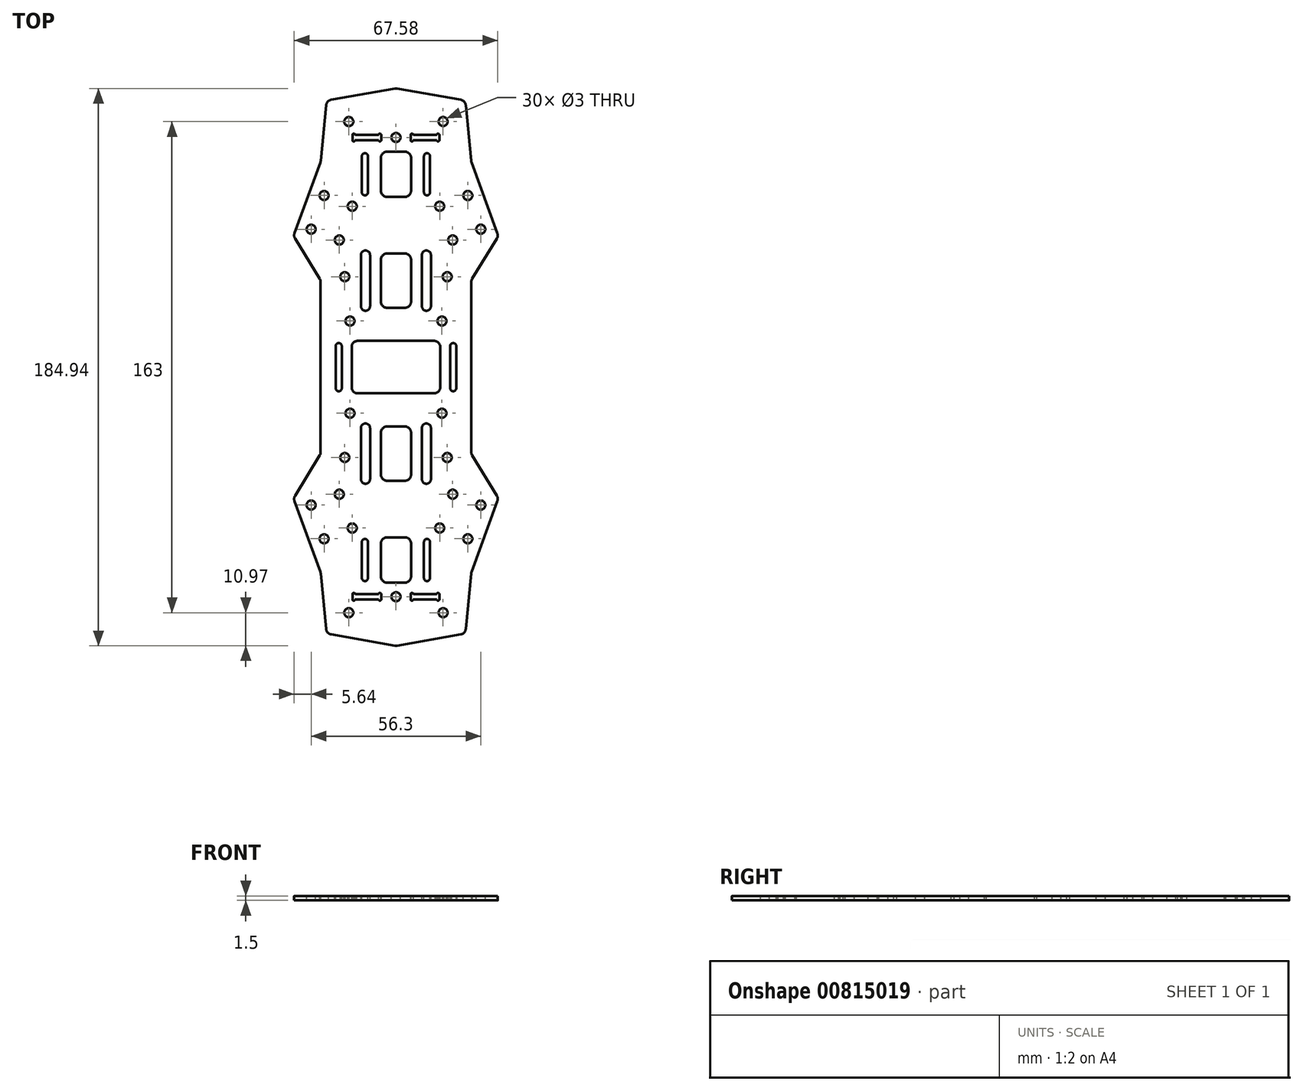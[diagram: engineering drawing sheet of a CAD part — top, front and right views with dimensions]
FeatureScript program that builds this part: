
annotation { "Feature Type Name" : "Feature", "Feature Type Description" : "" }
export const myFeature = defineFeature(function(context is Context, id is Id, definition is map)
    precondition{}
    {
        {
            var Q0;
            Q0=qCreatedBy(makeId("Top.planeOp"),FACE);
            var sketch = newSketch(context, id + "F0", { "sketchPlane" : qUnion([Q0])});
            skLineSegment(sketch, "E0.0.14", {"start": v(-25, 92.5) * mm, "end": v(-25, 63.7) * mm});
            skLineSegment(sketch, "E0.0.16", {"start": v(-25, 63.7) * mm, "end": v(-34, 49) * mm});
            skLineSegment(sketch, "E0.0.18", {"start": v(-34, 49) * mm, "end": v(-25, 24.3) * mm});
            skLineSegment(sketch, "E0.0.20", {"start": v(-25, 24.3) * mm, "end": v(-23, 4.06) * mm});
            skLineSegment(sketch, "E0.0.22", {"start": v(-23, 4.06) * mm, "end": v(0, 0) * mm});
            skLineSegment(sketch, "E0.0.23", {"start": v(0, 0) * mm, "end": v(23, 4.06) * mm});
            skLineSegment(sketch, "E0.0.25", {"start": v(23, 4.06) * mm, "end": v(25, 24.3) * mm});
            skLineSegment(sketch, "E0.0.27", {"start": v(25, 24.3) * mm, "end": v(34, 49) * mm});
            skLineSegment(sketch, "E0.0.29", {"start": v(34, 49) * mm, "end": v(25, 63.7) * mm});
            skLineSegment(sketch, "E0.0.31", {"start": v(25, 63.7) * mm, "end": v(25, 92.5) * mm});
            skLineSegment(sketch, "E1.bottom", {"start": v(34, 0) * mm, "end": v(-34, 0) * mm, "construction": true});
            skLineSegment(sketch, "E1.top", {"start": v(34, 185) * mm, "end": v(-34, 185) * mm, "construction": true});
            skLineSegment(sketch, "E1.left", {"start": v(-34, 0) * mm, "end": v(-34, 185) * mm, "construction": true});
            skLineSegment(sketch, "E1.right", {"start": v(34, 0) * mm, "end": v(34, 185) * mm, "construction": true});
            skPoint(sketch, "E2", {"position": v(0, 0) * mm});
            skLineSegment(sketch, "E3", {"start": v(0, 185) * mm, "end": v(0, 0) * mm, "construction": true});
            skLineSegment(sketch, "E4", {"start": v(-34, 92.5) * mm, "end": v(34, 92.5) * mm, "construction": true});
            skLineSegment(sketch, "E5.MirrorCS", {"start": v(-25, 92.5) * mm, "end": v(-25, 121.3) * mm});
            skLineSegment(sketch, "E6.MirrorCS", {"start": v(25, 121.3) * mm, "end": v(25, 92.5) * mm});
            skLineSegment(sketch, "E7.MirrorCS", {"start": v(34, 136) * mm, "end": v(25, 121.3) * mm});
            skLineSegment(sketch, "E8.MirrorCS", {"start": v(25, 160.7) * mm, "end": v(34, 136) * mm});
            skLineSegment(sketch, "E9.MirrorCS", {"start": v(23, 180.94) * mm, "end": v(25, 160.7) * mm});
            skLineSegment(sketch, "E10.MirrorCS", {"start": v(0, 185) * mm, "end": v(23, 180.94) * mm});
            skLineSegment(sketch, "E11.MirrorCS", {"start": v(-23, 180.94) * mm, "end": v(0, 185) * mm});
            skLineSegment(sketch, "E12.MirrorCS", {"start": v(-25, 160.7) * mm, "end": v(-23, 180.94) * mm});
            skLineSegment(sketch, "E13.MirrorCS", {"start": v(-34, 136) * mm, "end": v(-25, 160.7) * mm});
            skLineSegment(sketch, "E14.MirrorCS", {"start": v(-25, 121.3) * mm, "end": v(-34, 136) * mm});
            skPoint(sketch, "E15", {"position": v(0, 185) * mm});
            skSolve(sketch);
        }
        {
            var Q0;
            Q0=qSketchRegion(id+"F0",true);
            extrude(context, id + "F1", {"entities" : qUnion([Q0]), "depth" : 1.5 * mm, "offsetDistance" : 25 * mm});
        }
        {
            var Q0;
            Q0=makeQuery(id+"F1.opExtrude","CAP_FACE",FACE,{"disambiguationData":[OSD([sQuery(id+"F0.wireOp",EDGE,"E0.0.1"),sQuery(id+"F0.wireOp",EDGE,"E0.0.3"),sQuery(id+"F0.wireOp",EDGE,"E0.0.5"),sQuery(id+"F0.wireOp",EDGE,"E0.0.6"),sQuery(id+"F0.wireOp",EDGE,"E0.0.8"),sQuery(id+"F0.wireOp",EDGE,"E0.0.10"),sQuery(id+"F0.wireOp",EDGE,"E0.0.12"),sQuery(id+"F0.wireOp",EDGE,"E0.0.14"),sQuery(id+"F0.wireOp",EDGE,"E0.0.16"),sQuery(id+"F0.wireOp",EDGE,"E0.0.18"),sQuery(id+"F0.wireOp",EDGE,"E0.0.20"),sQuery(id+"F0.wireOp",EDGE,"E0.0.22"),sQuery(id+"F0.wireOp",EDGE,"E0.0.23"),sQuery(id+"F0.wireOp",EDGE,"E0.0.25"),sQuery(id+"F0.wireOp",EDGE,"E0.0.27"),sQuery(id+"F0.wireOp",EDGE,"E0.0.29"),sQuery(id+"F0.wireOp",EDGE,"E0.0.31"),sQuery(id+"F0.wireOp",EDGE,"E0.0.33")])],"isStart":false});
            var sketch = newSketch(context, id + "F2", { "sketchPlane" : qUnion([Q0])});
            skCircle(sketch, "E16.0", {"center": v(-15.65, 11) * mm, "radius": 1.5 * mm});
            skCircle(sketch, "E17.0", {"center": v(0, 16.3) * mm, "radius": 1.5 * mm});
            skCircle(sketch, "E17.9", {"center": v(15.65, 11) * mm, "radius": 1.5 * mm});
            skCircle(sketch, "E18.1", {"center": v(-23.85, 35.53) * mm, "radius": 1.5 * mm});
            skCircle(sketch, "E18.2", {"center": v(-28.15, 46.73) * mm, "radius": 1.5 * mm});
            skCircle(sketch, "E18.3", {"center": v(-14.51, 39.11) * mm, "radius": 1.5 * mm});
            skCircle(sketch, "E18.4", {"center": v(-18.81, 50.32) * mm, "radius": 1.5 * mm});
            skCircle(sketch, "E19.0", {"center": v(-17, 62.5) * mm, "radius": 1.5 * mm});
            skLineSegment(sketch, "E20", {"start": v(-10.3, 34.5) * mm, "end": v(-10.3, 22.5) * mm, "construction": true});
            skArc(sketch, "E21.0.startCap", {"start": v(-11.3, 34.5) * mm, "mid": v(-10.3, 35.5) * mm, "end": v(-9.3, 34.5) * mm});
            skArc(sketch, "E21.0.endCap", {"start": v(-9.3, 22.5) * mm, "mid": v(-10.3, 21.5) * mm, "end": v(-11.3, 22.5) * mm});
            skLineSegment(sketch, "E21.0.left", {"start": v(-9.3, 34.5) * mm, "end": v(-9.3, 22.5) * mm});
            skLineSegment(sketch, "E21.0.right", {"start": v(-11.3, 34.5) * mm, "end": v(-11.3, 22.5) * mm});
            skLineSegment(sketch, "E22", {"start": v(-19, 99.5) * mm, "end": v(-19, 85.5) * mm, "construction": true});
            skArc(sketch, "E23.0.startCap", {"start": v(-20, 99.5) * mm, "mid": v(-19, 100.5) * mm, "end": v(-18, 99.5) * mm});
            skArc(sketch, "E23.0.endCap", {"start": v(-18, 85.5) * mm, "mid": v(-19, 84.5) * mm, "end": v(-20, 85.5) * mm});
            skLineSegment(sketch, "E23.0.left", {"start": v(-18, 99.5) * mm, "end": v(-18, 85.5) * mm});
            skLineSegment(sketch, "E23.0.right", {"start": v(-20, 99.5) * mm, "end": v(-20, 85.5) * mm});
            skLineSegment(sketch, "E24.bottom", {"start": v(5, 21) * mm, "end": v(-5, 21) * mm});
            skLineSegment(sketch, "E24.top", {"start": v(5, 36) * mm, "end": v(-5, 36) * mm});
            skLineSegment(sketch, "E24.left", {"start": v(5, 21) * mm, "end": v(5, 36) * mm});
            skLineSegment(sketch, "E24.right", {"start": v(-5, 21) * mm, "end": v(-5, 36) * mm});
            skPoint(sketch, "E24.middle", {"position": v(0, 28.5) * mm});
            skLineSegment(sketch, "E25", {"start": v(0, 0) * mm, "end": v(0, 185) * mm, "construction": true});
            skLineSegment(sketch, "E26", {"start": v(61.94, 0) * mm, "end": v(-64, 0) * mm, "construction": true});
            skLineSegment(sketch, "E27", {"start": v(-46.28, 185) * mm, "end": v(44.52, 185) * mm, "construction": true});
            skPoint(sketch, "E28", {"position": v(0, 92.5) * mm});
            skLineSegment(sketch, "E29", {"start": v(-80.28, 92.5) * mm, "end": v(79, 92.5) * mm, "construction": true});
            skLineSegment(sketch, "E30", {"start": v(-10.1, 72.3) * mm, "end": v(-10.1, 55.3) * mm, "construction": true});
            skArc(sketch, "E31.0.startCap", {"start": v(-11.6, 72.3) * mm, "mid": v(-10.1, 73.8) * mm, "end": v(-8.6, 72.3) * mm});
            skArc(sketch, "E31.0.endCap", {"start": v(-8.6, 55.3) * mm, "mid": v(-10.1, 53.8) * mm, "end": v(-11.6, 55.3) * mm});
            skLineSegment(sketch, "E31.0.left", {"start": v(-8.6, 72.3) * mm, "end": v(-8.6, 55.3) * mm});
            skLineSegment(sketch, "E31.0.right", {"start": v(-11.6, 72.3) * mm, "end": v(-11.6, 55.3) * mm});
            skLineSegment(sketch, "E32.bottom", {"start": v(5, 54.8) * mm, "end": v(-5, 54.8) * mm});
            skLineSegment(sketch, "E32.top", {"start": v(5, 72.8) * mm, "end": v(-5, 72.8) * mm});
            skLineSegment(sketch, "E32.left", {"start": v(5, 54.8) * mm, "end": v(5, 72.8) * mm});
            skLineSegment(sketch, "E32.right", {"start": v(-5, 54.8) * mm, "end": v(-5, 72.8) * mm});
            skPoint(sketch, "E32.middle", {"position": v(0, 63.8) * mm});
            skArc(sketch, "E33.MirrorCS", {"start": v(-18, 99.5) * mm, "mid": v(-19, 100.5) * mm, "end": v(-20, 99.5) * mm});
            skArc(sketch, "E34.MirrorCS", {"start": v(-20, 85.5) * mm, "mid": v(-19, 84.5) * mm, "end": v(-18, 85.5) * mm});
            skLineSegment(sketch, "E35.bottom", {"start": v(14.7, 83.8) * mm, "end": v(-14.7, 83.8) * mm});
            skLineSegment(sketch, "E35.top", {"start": v(14.7, 101.2) * mm, "end": v(-14.7, 101.2) * mm});
            skLineSegment(sketch, "E35.left", {"start": v(14.7, 83.8) * mm, "end": v(14.7, 101.2) * mm});
            skLineSegment(sketch, "E35.right", {"start": v(-14.7, 83.8) * mm, "end": v(-14.7, 101.2) * mm});
            skCircle(sketch, "E36", {"center": v(-15.25, 77.2) * mm, "radius": 1.5 * mm});
            skLineSegment(sketch, "E37", {"start": v(-13.98, 17.18) * mm, "end": v(-13.98, 15.43) * mm, "construction": true});
            skArc(sketch, "E38.0.startCap", {"start": v(-14.4, 17.18) * mm, "mid": v(-13.98, 17.6) * mm, "end": v(-13.55, 17.18) * mm});
            skArc(sketch, "E38.0.endCap", {"start": v(-13.55, 15.43) * mm, "mid": v(-13.98, 15) * mm, "end": v(-14.4, 15.43) * mm});
            skLineSegment(sketch, "E38.0.left", {"start": v(-13.55, 17.18) * mm, "end": v(-13.55, 15.43) * mm});
            skLineSegment(sketch, "E38.0.right", {"start": v(-14.4, 17.18) * mm, "end": v(-14.4, 15.43) * mm});
            skLineSegment(sketch, "E39", {"start": v(-5.33, 17.18) * mm, "end": v(-5.33, 15.43) * mm, "construction": true});
            skArc(sketch, "E40.0.startCap", {"start": v(-5.75, 17.18) * mm, "mid": v(-5.33, 17.6) * mm, "end": v(-4.9, 17.18) * mm});
            skArc(sketch, "E40.0.endCap", {"start": v(-4.9, 15.43) * mm, "mid": v(-5.33, 15) * mm, "end": v(-5.75, 15.43) * mm});
            skLineSegment(sketch, "E40.0.left", {"start": v(-4.9, 17.18) * mm, "end": v(-4.9, 15.43) * mm});
            skLineSegment(sketch, "E40.0.right", {"start": v(-5.75, 17.18) * mm, "end": v(-5.75, 15.43) * mm});
            skLineSegment(sketch, "E41", {"start": v(-13.55, 17.18) * mm, "end": v(-5.75, 17.18) * mm});
            skLineSegment(sketch, "E42", {"start": v(-13.55, 15.43) * mm, "end": v(-5.75, 15.43) * mm});
            skLineSegment(sketch, "E43", {"start": v(-13.55, 15.43) * mm, "end": v(-5.75, 17.18) * mm, "construction": true});
            skPoint(sketch, "E44", {"position": v(-9.65, 16.3) * mm});
            skArc(sketch, "E45.MirrorCS", {"start": v(13.55, 15.43) * mm, "mid": v(13.97, 15) * mm, "end": v(14.4, 15.43) * mm});
            skArc(sketch, "E46.MirrorCS", {"start": v(4.9, 15.43) * mm, "mid": v(5.32, 15) * mm, "end": v(5.75, 15.43) * mm});
            skLineSegment(sketch, "E47.MirrorCS", {"start": v(13.55, 15.43) * mm, "end": v(5.75, 15.43) * mm});
            skLineSegment(sketch, "E48.MirrorCS", {"start": v(4.9, 17.18) * mm, "end": v(4.9, 15.43) * mm});
            skArc(sketch, "E49.MirrorCS", {"start": v(5.75, 17.18) * mm, "mid": v(5.32, 17.6) * mm, "end": v(4.9, 17.18) * mm});
            skLineSegment(sketch, "E50.MirrorCS", {"start": v(5.32, 17.18) * mm, "end": v(5.32, 15.43) * mm, "construction": true});
            skLineSegment(sketch, "E51.MirrorCS", {"start": v(5.75, 17.18) * mm, "end": v(5.75, 15.43) * mm});
            skLineSegment(sketch, "E52.MirrorCS", {"start": v(13.55, 15.43) * mm, "end": v(5.75, 17.18) * mm, "construction": true});
            skLineSegment(sketch, "E53.MirrorCS", {"start": v(13.97, 17.18) * mm, "end": v(13.97, 15.43) * mm, "construction": true});
            skPoint(sketch, "E54.MirrorP", {"position": v(9.65, 16.3) * mm});
            skLineSegment(sketch, "E55.MirrorCS", {"start": v(14.4, 17.18) * mm, "end": v(14.4, 15.43) * mm});
            skLineSegment(sketch, "E56.MirrorCS", {"start": v(13.55, 17.18) * mm, "end": v(5.75, 17.18) * mm});
            skArc(sketch, "E57.MirrorCS", {"start": v(14.4, 17.18) * mm, "mid": v(13.97, 17.6) * mm, "end": v(13.55, 17.18) * mm});
            skLineSegment(sketch, "E58.MirrorCS", {"start": v(13.55, 17.18) * mm, "end": v(13.55, 15.43) * mm});
            skPoint(sketch, "E59", {"position": v(-10.3, 28.5) * mm});
            skArc(sketch, "E60.MirrorCS", {"start": v(9.3, 22.5) * mm, "mid": v(10.3, 21.5) * mm, "end": v(11.3, 22.5) * mm});
            skArc(sketch, "E61.MirrorCS", {"start": v(11.3, 34.5) * mm, "mid": v(10.3, 35.5) * mm, "end": v(9.3, 34.5) * mm});
            skLineSegment(sketch, "E62.MirrorCS", {"start": v(11.3, 34.5) * mm, "end": v(11.3, 22.5) * mm});
            skLineSegment(sketch, "E63.MirrorCS", {"start": v(10.3, 34.5) * mm, "end": v(10.3, 22.5) * mm, "construction": true});
            skPoint(sketch, "E64.MirrorP", {"position": v(10.3, 28.5) * mm});
            skLineSegment(sketch, "E65.MirrorCS", {"start": v(9.3, 34.5) * mm, "end": v(9.3, 22.5) * mm});
            skLineSegment(sketch, "E66.bottom", {"start": v(-23.85, 35.53) * mm, "end": v(-28.15, 46.73) * mm, "construction": true});
            skLineSegment(sketch, "E66.top", {"start": v(-14.51, 39.11) * mm, "end": v(-18.81, 50.32) * mm, "construction": true});
            skLineSegment(sketch, "E66.left", {"start": v(-23.85, 35.53) * mm, "end": v(-14.51, 39.11) * mm, "construction": true});
            skLineSegment(sketch, "E66.right", {"start": v(-28.15, 46.73) * mm, "end": v(-18.81, 50.32) * mm, "construction": true});
            skPoint(sketch, "E66.middle", {"position": v(-21.33, 42.92) * mm});
            skPoint(sketch, "E67.MirrorP", {"position": v(21.33, 42.92) * mm});
            skCircle(sketch, "E68.MirrorC", {"center": v(18.81, 50.32) * mm, "radius": 1.5 * mm});
            skCircle(sketch, "E69.MirrorC", {"center": v(28.15, 46.73) * mm, "radius": 1.5 * mm});
            skCircle(sketch, "E70.MirrorC", {"center": v(14.51, 39.11) * mm, "radius": 1.5 * mm});
            skCircle(sketch, "E71.MirrorC", {"center": v(23.85, 35.53) * mm, "radius": 1.5 * mm});
            skPoint(sketch, "E72", {"position": v(-10.1, 63.8) * mm});
            skPoint(sketch, "E73.MirrorP", {"position": v(10.1, 63.8) * mm});
            skArc(sketch, "E74.MirrorCS", {"start": v(11.6, 72.3) * mm, "mid": v(10.1, 73.8) * mm, "end": v(8.6, 72.3) * mm});
            skLineSegment(sketch, "E75.MirrorCS", {"start": v(11.6, 72.3) * mm, "end": v(11.6, 55.3) * mm});
            skLineSegment(sketch, "E76.MirrorCS", {"start": v(8.6, 72.3) * mm, "end": v(8.6, 55.3) * mm});
            skArc(sketch, "E77.MirrorCS", {"start": v(8.6, 55.3) * mm, "mid": v(10.1, 53.8) * mm, "end": v(11.6, 55.3) * mm});
            skLineSegment(sketch, "E78.MirrorCS", {"start": v(10.1, 72.3) * mm, "end": v(10.1, 55.3) * mm, "construction": true});
            skCircle(sketch, "E79.MirrorC", {"center": v(17, 62.5) * mm, "radius": 1.5 * mm});
            skLineSegment(sketch, "E80.MirrorCS", {"start": v(20, 99.5) * mm, "end": v(20, 85.5) * mm});
            skArc(sketch, "E81.MirrorCS", {"start": v(18, 99.5) * mm, "mid": v(19, 100.5) * mm, "end": v(20, 99.5) * mm});
            skLineSegment(sketch, "E82.MirrorCS", {"start": v(18, 99.5) * mm, "end": v(18, 85.5) * mm});
            skArc(sketch, "E83.MirrorCS", {"start": v(18, 85.5) * mm, "mid": v(19, 84.5) * mm, "end": v(20, 85.5) * mm});
            skArc(sketch, "E84.MirrorCS", {"start": v(20, 85.5) * mm, "mid": v(19, 84.5) * mm, "end": v(18, 85.5) * mm});
            skArc(sketch, "E85.MirrorCS", {"start": v(20, 99.5) * mm, "mid": v(19, 100.5) * mm, "end": v(18, 99.5) * mm});
            skLineSegment(sketch, "E86.MirrorCS", {"start": v(19, 99.5) * mm, "end": v(19, 85.5) * mm, "construction": true});
            skCircle(sketch, "E87.MirrorC", {"center": v(15.25, 77.2) * mm, "radius": 1.5 * mm});
            skArc(sketch, "E88.MirrorCS", {"start": v(-11.3, 150.5) * mm, "mid": v(-10.3, 149.5) * mm, "end": v(-9.3, 150.5) * mm});
            skArc(sketch, "E89.MirrorCS", {"start": v(8.6, 129.7) * mm, "mid": v(10.1, 131.2) * mm, "end": v(11.6, 129.7) * mm});
            skArc(sketch, "E90.MirrorCS", {"start": v(-8.6, 129.7) * mm, "mid": v(-10.1, 131.2) * mm, "end": v(-11.6, 129.7) * mm});
            skCircle(sketch, "E91.MirrorC", {"center": v(-14.51, 145.89) * mm, "radius": 1.5 * mm});
            skCircle(sketch, "E92.MirrorC", {"center": v(-18.81, 134.68) * mm, "radius": 1.5 * mm});
            skArc(sketch, "E93.MirrorCS", {"start": v(-11.6, 112.7) * mm, "mid": v(-10.1, 111.2) * mm, "end": v(-8.6, 112.7) * mm});
            skArc(sketch, "E94.MirrorCS", {"start": v(11.6, 112.7) * mm, "mid": v(10.1, 111.2) * mm, "end": v(8.6, 112.7) * mm});
            skArc(sketch, "E95.MirrorCS", {"start": v(11.3, 150.5) * mm, "mid": v(10.3, 149.5) * mm, "end": v(9.3, 150.5) * mm});
            skCircle(sketch, "E96.MirrorC", {"center": v(18.81, 134.68) * mm, "radius": 1.5 * mm});
            skCircle(sketch, "E97.MirrorC", {"center": v(15.25, 107.8) * mm, "radius": 1.5 * mm});
            skCircle(sketch, "E98.MirrorC", {"center": v(-15.25, 107.8) * mm, "radius": 1.5 * mm});
            skCircle(sketch, "E99.MirrorC", {"center": v(17, 122.5) * mm, "radius": 1.5 * mm});
            skCircle(sketch, "E100.MirrorC", {"center": v(-17, 122.5) * mm, "radius": 1.5 * mm});
            skCircle(sketch, "E101.MirrorC", {"center": v(14.51, 145.89) * mm, "radius": 1.5 * mm});
            skLineSegment(sketch, "E102.MirrorCS", {"start": v(8.6, 112.7) * mm, "end": v(8.6, 129.7) * mm});
            skLineSegment(sketch, "E103.MirrorCS", {"start": v(-8.6, 112.7) * mm, "end": v(-8.6, 129.7) * mm});
            skPoint(sketch, "E104.MirrorP", {"position": v(0, 121.2) * mm});
            skLineSegment(sketch, "E105.MirrorCS", {"start": v(-5, 130.2) * mm, "end": v(-5, 112.2) * mm});
            skLineSegment(sketch, "E106.MirrorCS", {"start": v(5, 112.2) * mm, "end": v(-5, 112.2) * mm});
            skLineSegment(sketch, "E107.MirrorCS", {"start": v(-11.6, 112.7) * mm, "end": v(-11.6, 129.7) * mm});
            skLineSegment(sketch, "E108.MirrorCS", {"start": v(10.1, 112.7) * mm, "end": v(10.1, 129.7) * mm, "construction": true});
            skLineSegment(sketch, "E109.MirrorCS", {"start": v(11.6, 112.7) * mm, "end": v(11.6, 129.7) * mm});
            skLineSegment(sketch, "E110.MirrorCS", {"start": v(-10.1, 112.7) * mm, "end": v(-10.1, 129.7) * mm, "construction": true});
            skPoint(sketch, "E111.MirrorP", {"position": v(-10.1, 121.2) * mm});
            skLineSegment(sketch, "E112.MirrorCS", {"start": v(5, 130.2) * mm, "end": v(-5, 130.2) * mm});
            skLineSegment(sketch, "E113.MirrorCS", {"start": v(5, 149) * mm, "end": v(-5, 149) * mm});
            skPoint(sketch, "E114.MirrorP", {"position": v(10.1, 121.2) * mm});
            skLineSegment(sketch, "E115.MirrorCS", {"start": v(5, 130.2) * mm, "end": v(5, 112.2) * mm});
            skCircle(sketch, "E116.MirrorC", {"center": v(-23.85, 149.47) * mm, "radius": 1.5 * mm});
            skCircle(sketch, "E117.MirrorC", {"center": v(-28.15, 138.27) * mm, "radius": 1.5 * mm});
            skCircle(sketch, "E118.MirrorC", {"center": v(28.15, 138.27) * mm, "radius": 1.5 * mm});
            skCircle(sketch, "E119.MirrorC", {"center": v(23.85, 149.47) * mm, "radius": 1.5 * mm});
            skArc(sketch, "E120.MirrorCS", {"start": v(-9.3, 162.5) * mm, "mid": v(-10.3, 163.5) * mm, "end": v(-11.3, 162.5) * mm});
            skArc(sketch, "E121.MirrorCS", {"start": v(9.3, 162.5) * mm, "mid": v(10.3, 163.5) * mm, "end": v(11.3, 162.5) * mm});
            skLineSegment(sketch, "E122.MirrorCS", {"start": v(-5, 164) * mm, "end": v(-5, 149) * mm});
            skLineSegment(sketch, "E123.MirrorCS", {"start": v(9.3, 150.5) * mm, "end": v(9.3, 162.5) * mm});
            skPoint(sketch, "E124.MirrorP", {"position": v(0, 156.5) * mm});
            skPoint(sketch, "E125.MirrorP", {"position": v(10.3, 156.5) * mm});
            skLineSegment(sketch, "E126.MirrorCS", {"start": v(11.3, 150.5) * mm, "end": v(11.3, 162.5) * mm});
            skLineSegment(sketch, "E127.MirrorCS", {"start": v(5, 164) * mm, "end": v(5, 149) * mm});
            skLineSegment(sketch, "E128.MirrorCS", {"start": v(-11.3, 150.5) * mm, "end": v(-11.3, 162.5) * mm});
            skLineSegment(sketch, "E129.MirrorCS", {"start": v(5, 164) * mm, "end": v(-5, 164) * mm});
            skLineSegment(sketch, "E130.MirrorCS", {"start": v(-10.3, 150.5) * mm, "end": v(-10.3, 162.5) * mm, "construction": true});
            skPoint(sketch, "E131.MirrorP", {"position": v(-10.3, 156.5) * mm});
            skLineSegment(sketch, "E132.MirrorCS", {"start": v(10.3, 150.5) * mm, "end": v(10.3, 162.5) * mm, "construction": true});
            skLineSegment(sketch, "E133.MirrorCS", {"start": v(-9.3, 150.5) * mm, "end": v(-9.3, 162.5) * mm});
            skLineSegment(sketch, "E134.MirrorCS", {"start": v(-5.75, 167.83) * mm, "end": v(-5.75, 169.58) * mm});
            skLineSegment(sketch, "E135.MirrorCS", {"start": v(13.97, 167.82) * mm, "end": v(13.97, 169.58) * mm, "construction": true});
            skArc(sketch, "E136.MirrorCS", {"start": v(14.4, 167.82) * mm, "mid": v(13.97, 167.4) * mm, "end": v(13.55, 167.82) * mm});
            skLineSegment(sketch, "E137.MirrorCS", {"start": v(14.4, 167.82) * mm, "end": v(14.4, 169.58) * mm});
            skArc(sketch, "E138.MirrorCS", {"start": v(-5.75, 167.83) * mm, "mid": v(-5.33, 167.4) * mm, "end": v(-4.9, 167.83) * mm});
            skLineSegment(sketch, "E139.MirrorCS", {"start": v(13.55, 167.82) * mm, "end": v(13.55, 169.58) * mm});
            skArc(sketch, "E140.MirrorCS", {"start": v(13.55, 169.58) * mm, "mid": v(13.97, 170) * mm, "end": v(14.4, 169.58) * mm});
            skArc(sketch, "E141.MirrorCS", {"start": v(5.75, 167.83) * mm, "mid": v(5.32, 167.4) * mm, "end": v(4.9, 167.83) * mm});
            skArc(sketch, "E142.MirrorCS", {"start": v(-13.55, 169.58) * mm, "mid": v(-13.98, 170) * mm, "end": v(-14.4, 169.58) * mm});
            skLineSegment(sketch, "E143.MirrorCS", {"start": v(-13.98, 167.83) * mm, "end": v(-13.98, 169.58) * mm, "construction": true});
            skLineSegment(sketch, "E144.MirrorCS", {"start": v(4.9, 167.83) * mm, "end": v(4.9, 169.58) * mm});
            skLineSegment(sketch, "E145.MirrorCS", {"start": v(5.75, 167.83) * mm, "end": v(5.75, 169.58) * mm});
            skLineSegment(sketch, "E146.MirrorCS", {"start": v(-5.33, 167.83) * mm, "end": v(-5.33, 169.58) * mm, "construction": true});
            skLineSegment(sketch, "E147.MirrorCS", {"start": v(5.32, 167.83) * mm, "end": v(5.32, 169.58) * mm, "construction": true});
            skArc(sketch, "E148.MirrorCS", {"start": v(-4.9, 169.58) * mm, "mid": v(-5.33, 170) * mm, "end": v(-5.75, 169.58) * mm});
            skArc(sketch, "E149.MirrorCS", {"start": v(-14.4, 167.83) * mm, "mid": v(-13.98, 167.4) * mm, "end": v(-13.55, 167.83) * mm});
            skLineSegment(sketch, "E150.MirrorCS", {"start": v(-13.55, 167.83) * mm, "end": v(-13.55, 169.58) * mm});
            skLineSegment(sketch, "E151.MirrorCS", {"start": v(-14.4, 167.83) * mm, "end": v(-14.4, 169.58) * mm});
            skLineSegment(sketch, "E152.MirrorCS", {"start": v(-4.9, 167.83) * mm, "end": v(-4.9, 169.58) * mm});
            skArc(sketch, "E153.MirrorCS", {"start": v(4.9, 169.58) * mm, "mid": v(5.32, 170) * mm, "end": v(5.75, 169.58) * mm});
            skPoint(sketch, "E154.MirrorP", {"position": v(-9.65, 168.7) * mm});
            skPoint(sketch, "E155.MirrorP", {"position": v(9.65, 168.7) * mm});
            skCircle(sketch, "E156.MirrorC", {"center": v(-15.65, 174) * mm, "radius": 1.5 * mm});
            skLineSegment(sketch, "E157.MirrorCS", {"start": v(13.55, 169.58) * mm, "end": v(5.75, 169.58) * mm});
            skCircle(sketch, "E158.MirrorC", {"center": v(15.65, 174) * mm, "radius": 1.5 * mm});
            skLineSegment(sketch, "E159.MirrorCS", {"start": v(-13.55, 169.58) * mm, "end": v(-5.75, 167.82) * mm, "construction": true});
            skCircle(sketch, "E160.MirrorC", {"center": v(0, 168.7) * mm, "radius": 1.5 * mm});
            skLineSegment(sketch, "E161.MirrorCS", {"start": v(13.55, 169.58) * mm, "end": v(5.75, 167.83) * mm, "construction": true});
            skLineSegment(sketch, "E162.MirrorCS", {"start": v(13.55, 167.82) * mm, "end": v(5.75, 167.82) * mm});
            skLineSegment(sketch, "E163.MirrorCS", {"start": v(-13.55, 169.58) * mm, "end": v(-5.75, 169.58) * mm});
            skLineSegment(sketch, "E164.MirrorCS", {"start": v(-13.55, 167.83) * mm, "end": v(-5.75, 167.83) * mm});
            skSolve(sketch);
        }
        {
            var Q0;
            Q0=qSketchRegion(id+"F2",true);
            extrude(context, id + "F3", {"entities" : qUnion([Q0]), "operationType" : NewBodyOperationType.REMOVE, "endBound" : BoundingType.UP_TO_NEXT, "oppositeDirection" : true, "depth" : 25 * mm, "offsetDistance" : 25 * mm});
        }
        {
            var Q0;
            Q0=makeQuery(id+"F1.opExtrude","SWEPT_EDGE",EDGE,{"disambiguationData":[OSD([sQuery(id+"F0.wireOp",EDGE,"E0.0.23"),sQuery(id+"F0.wireOp",EDGE,"E0.0.25")])]});
            var Q1;
            Q1=makeQuery(id+"F1.opExtrude","SWEPT_EDGE",EDGE,{"disambiguationData":[OSD([sQuery(id+"F0.wireOp",EDGE,"E0.0.25"),sQuery(id+"F0.wireOp",EDGE,"E0.0.27")])]});
            var Q2;
            Q2=makeQuery(id+"F1.opExtrude","SWEPT_EDGE",EDGE,{"disambiguationData":[OSD([sQuery(id+"F0.wireOp",EDGE,"E0.0.27"),sQuery(id+"F0.wireOp",EDGE,"E0.0.29")])]});
            var Q3;
            Q3=makeQuery(id+"F1.opExtrude","SWEPT_EDGE",EDGE,{"disambiguationData":[OSD([sQuery(id+"F0.wireOp",EDGE,"E0.0.29"),sQuery(id+"F0.wireOp",EDGE,"E0.0.31")])]});
            var Q4;
            Q4=makeQuery(id+"F1.opExtrude","SWEPT_EDGE",EDGE,{"disambiguationData":[OSD([sQuery(id+"F0.wireOp",EDGE,"E6.MirrorCS"),sQuery(id+"F0.wireOp",EDGE,"E7.MirrorCS")])]});
            var Q5;
            Q5=makeQuery(id+"F1.opExtrude","SWEPT_EDGE",EDGE,{"disambiguationData":[OSD([sQuery(id+"F0.wireOp",EDGE,"E7.MirrorCS"),sQuery(id+"F0.wireOp",EDGE,"E8.MirrorCS")])]});
            var Q6;
            Q6=makeQuery(id+"F1.opExtrude","SWEPT_EDGE",EDGE,{"disambiguationData":[OSD([sQuery(id+"F0.wireOp",EDGE,"E8.MirrorCS"),sQuery(id+"F0.wireOp",EDGE,"E9.MirrorCS")])]});
            var Q7;
            Q7=makeQuery(id+"F1.opExtrude","SWEPT_EDGE",EDGE,{"disambiguationData":[OSD([sQuery(id+"F0.wireOp",EDGE,"E9.MirrorCS"),sQuery(id+"F0.wireOp",EDGE,"E10.MirrorCS")])]});
            var Q8;
            Q8=makeQuery(id+"F1.opExtrude","SWEPT_EDGE",EDGE,{"disambiguationData":[OSD([sQuery(id+"F0.wireOp",EDGE,"E10.MirrorCS"),sQuery(id+"F0.wireOp",EDGE,"E11.MirrorCS")])]});
            var Q9;
            Q9=makeQuery(id+"F1.opExtrude","SWEPT_EDGE",EDGE,{"disambiguationData":[OSD([sQuery(id+"F0.wireOp",EDGE,"E11.MirrorCS"),sQuery(id+"F0.wireOp",EDGE,"E12.MirrorCS")])]});
            var Q10;
            Q10=makeQuery(id+"F1.opExtrude","SWEPT_EDGE",EDGE,{"disambiguationData":[OSD([sQuery(id+"F0.wireOp",EDGE,"E12.MirrorCS"),sQuery(id+"F0.wireOp",EDGE,"E13.MirrorCS")])]});
            var Q11;
            Q11=makeQuery(id+"F1.opExtrude","SWEPT_EDGE",EDGE,{"disambiguationData":[OSD([sQuery(id+"F0.wireOp",EDGE,"E13.MirrorCS"),sQuery(id+"F0.wireOp",EDGE,"E14.MirrorCS")])]});
            var Q12;
            Q12=makeQuery(id+"F1.opExtrude","SWEPT_EDGE",EDGE,{"disambiguationData":[OSD([sQuery(id+"F0.wireOp",EDGE,"E5.MirrorCS"),sQuery(id+"F0.wireOp",EDGE,"E14.MirrorCS")])]});
            var Q13;
            Q13=makeQuery(id+"F1.opExtrude","SWEPT_EDGE",EDGE,{"disambiguationData":[OSD([sQuery(id+"F0.wireOp",EDGE,"E0.0.14"),sQuery(id+"F0.wireOp",EDGE,"E0.0.16")])]});
            var Q14;
            Q14=makeQuery(id+"F1.opExtrude","SWEPT_EDGE",EDGE,{"disambiguationData":[OSD([sQuery(id+"F0.wireOp",EDGE,"E0.0.16"),sQuery(id+"F0.wireOp",EDGE,"E0.0.18")])]});
            var Q15;
            Q15=makeQuery(id+"F1.opExtrude","SWEPT_EDGE",EDGE,{"disambiguationData":[OSD([sQuery(id+"F0.wireOp",EDGE,"E0.0.18"),sQuery(id+"F0.wireOp",EDGE,"E0.0.20")])]});
            var Q16;
            Q16=makeQuery(id+"F1.opExtrude","SWEPT_EDGE",EDGE,{"disambiguationData":[OSD([sQuery(id+"F0.wireOp",EDGE,"E0.0.20"),sQuery(id+"F0.wireOp",EDGE,"E0.0.22")])]});
            var Q17;
            Q17=makeQuery(id+"F1.opExtrude","SWEPT_EDGE",EDGE,{"disambiguationData":[OSD([sQuery(id+"F0.wireOp",EDGE,"E0.0.22"),sQuery(id+"F0.wireOp",EDGE,"E0.0.23")])]});
            fillet(context, id + "F4", {"entities" : qUnion([Q0, Q1, Q2, Q3, Q4, Q5, Q6, Q7, Q8, Q9, Q10, Q11, Q12, Q13, Q14, Q15, Q16, Q17]), "radius" : 2 * mm, "tangentPropagation" : true, "allowEdgeOverflow" : false});
        }
        {
            var Q0;
            Q0=makeQuery(id+"F3.boolean.opBoolean","COPY",EDGE,{"derivedFrom":makeQuery(id+"F3.opExtrude","SWEPT_EDGE",EDGE,{"disambiguationData":[OSD([sQuery(id+"F2.wireOp",EDGE,"E24.bottom"),sQuery(id+"F2.wireOp",EDGE,"E24.left")])]})});
            var Q1;
            Q1=makeQuery(id+"F3.boolean.opBoolean","COPY",EDGE,{"derivedFrom":makeQuery(id+"F3.opExtrude","SWEPT_EDGE",EDGE,{"disambiguationData":[OSD([sQuery(id+"F2.wireOp",EDGE,"E32.bottom"),sQuery(id+"F2.wireOp",EDGE,"E32.left")])]})});
            var Q2;
            Q2=makeQuery(id+"F3.boolean.opBoolean","COPY",EDGE,{"derivedFrom":makeQuery(id+"F3.opExtrude","SWEPT_EDGE",EDGE,{"disambiguationData":[OSD([sQuery(id+"F2.wireOp",EDGE,"E24.top"),sQuery(id+"F2.wireOp",EDGE,"E24.right")])]})});
            var Q3;
            Q3=makeQuery(id+"F3.boolean.opBoolean","COPY",EDGE,{"derivedFrom":makeQuery(id+"F3.opExtrude","SWEPT_EDGE",EDGE,{"disambiguationData":[OSD([sQuery(id+"F2.wireOp",EDGE,"E32.top"),sQuery(id+"F2.wireOp",EDGE,"E32.right")])]})});
            var Q4;
            Q4=makeQuery(id+"F3.boolean.opBoolean","COPY",EDGE,{"derivedFrom":makeQuery(id+"F3.opExtrude","SWEPT_EDGE",EDGE,{"disambiguationData":[OSD([sQuery(id+"F2.wireOp",EDGE,"E32.top"),sQuery(id+"F2.wireOp",EDGE,"E32.left")])]})});
            var Q5;
            Q5=makeQuery(id+"F3.boolean.opBoolean","COPY",EDGE,{"derivedFrom":makeQuery(id+"F3.opExtrude","SWEPT_EDGE",EDGE,{"disambiguationData":[OSD([sQuery(id+"F2.wireOp",EDGE,"E32.bottom"),sQuery(id+"F2.wireOp",EDGE,"E32.right")])]})});
            var Q6;
            Q6=makeQuery(id+"F3.boolean.opBoolean","COPY",EDGE,{"derivedFrom":makeQuery(id+"F3.opExtrude","SWEPT_EDGE",EDGE,{"disambiguationData":[OSD([sQuery(id+"F2.wireOp",EDGE,"E24.bottom"),sQuery(id+"F2.wireOp",EDGE,"E24.right")])]})});
            var Q7;
            Q7=makeQuery(id+"F3.boolean.opBoolean","COPY",EDGE,{"derivedFrom":makeQuery(id+"F3.opExtrude","SWEPT_EDGE",EDGE,{"disambiguationData":[OSD([sQuery(id+"F2.wireOp",EDGE,"E24.top"),sQuery(id+"F2.wireOp",EDGE,"E24.left")])]})});
            var Q8;
            Q8=makeQuery(id+"F3.boolean.opBoolean","COPY",EDGE,{"derivedFrom":makeQuery(id+"F3.opExtrude","SWEPT_EDGE",EDGE,{"disambiguationData":[OSD([sQuery(id+"F2.wireOp",EDGE,"E35.bottom"),sQuery(id+"F2.wireOp",EDGE,"E35.right")])]})});
            var Q9;
            Q9=makeQuery(id+"F3.boolean.opBoolean","COPY",EDGE,{"derivedFrom":makeQuery(id+"F3.opExtrude","SWEPT_EDGE",EDGE,{"disambiguationData":[OSD([sQuery(id+"F2.wireOp",EDGE,"E35.top"),sQuery(id+"F2.wireOp",EDGE,"E35.right")])]})});
            var Q10;
            Q10=makeQuery(id+"F3.boolean.opBoolean","COPY",EDGE,{"derivedFrom":makeQuery(id+"F3.opExtrude","SWEPT_EDGE",EDGE,{"disambiguationData":[OSD([sQuery(id+"F2.wireOp",EDGE,"E35.top"),sQuery(id+"F2.wireOp",EDGE,"E35.left")])]})});
            var Q11;
            Q11=makeQuery(id+"F3.boolean.opBoolean","COPY",EDGE,{"derivedFrom":makeQuery(id+"F3.opExtrude","SWEPT_EDGE",EDGE,{"disambiguationData":[OSD([sQuery(id+"F2.wireOp",EDGE,"E35.bottom"),sQuery(id+"F2.wireOp",EDGE,"E35.left")])]})});
            var Q12;
            Q12=makeQuery(id+"F3.boolean.opBoolean","COPY",EDGE,{"derivedFrom":makeQuery(id+"F3.opExtrude","SWEPT_EDGE",EDGE,{"disambiguationData":[OSD([sQuery(id+"F2.wireOp",EDGE,"E106.MirrorCS"),sQuery(id+"F2.wireOp",EDGE,"E115.MirrorCS")])]})});
            var Q13;
            Q13=makeQuery(id+"F3.boolean.opBoolean","COPY",EDGE,{"derivedFrom":makeQuery(id+"F3.opExtrude","SWEPT_EDGE",EDGE,{"disambiguationData":[OSD([sQuery(id+"F2.wireOp",EDGE,"E105.MirrorCS"),sQuery(id+"F2.wireOp",EDGE,"E106.MirrorCS")])]})});
            var Q14;
            Q14=makeQuery(id+"F3.boolean.opBoolean","COPY",EDGE,{"derivedFrom":makeQuery(id+"F3.opExtrude","SWEPT_EDGE",EDGE,{"disambiguationData":[OSD([sQuery(id+"F2.wireOp",EDGE,"E112.MirrorCS"),sQuery(id+"F2.wireOp",EDGE,"E115.MirrorCS")])]})});
            var Q15;
            Q15=makeQuery(id+"F3.boolean.opBoolean","COPY",EDGE,{"derivedFrom":makeQuery(id+"F3.opExtrude","SWEPT_EDGE",EDGE,{"disambiguationData":[OSD([sQuery(id+"F2.wireOp",EDGE,"E105.MirrorCS"),sQuery(id+"F2.wireOp",EDGE,"E112.MirrorCS")])]})});
            var Q16;
            Q16=makeQuery(id+"F3.boolean.opBoolean","COPY",EDGE,{"derivedFrom":makeQuery(id+"F3.opExtrude","SWEPT_EDGE",EDGE,{"disambiguationData":[OSD([sQuery(id+"F2.wireOp",EDGE,"E127.MirrorCS"),sQuery(id+"F2.wireOp",EDGE,"E113.MirrorCS")])]})});
            var Q17;
            Q17=makeQuery(id+"F3.boolean.opBoolean","COPY",EDGE,{"derivedFrom":makeQuery(id+"F3.opExtrude","SWEPT_EDGE",EDGE,{"disambiguationData":[OSD([sQuery(id+"F2.wireOp",EDGE,"E122.MirrorCS"),sQuery(id+"F2.wireOp",EDGE,"E113.MirrorCS")])]})});
            var Q18;
            Q18=makeQuery(id+"F3.boolean.opBoolean","COPY",EDGE,{"derivedFrom":makeQuery(id+"F3.opExtrude","SWEPT_EDGE",EDGE,{"disambiguationData":[OSD([sQuery(id+"F2.wireOp",EDGE,"E122.MirrorCS"),sQuery(id+"F2.wireOp",EDGE,"E129.MirrorCS")])]})});
            var Q19;
            Q19=makeQuery(id+"F3.boolean.opBoolean","COPY",EDGE,{"derivedFrom":makeQuery(id+"F3.opExtrude","SWEPT_EDGE",EDGE,{"disambiguationData":[OSD([sQuery(id+"F2.wireOp",EDGE,"E127.MirrorCS"),sQuery(id+"F2.wireOp",EDGE,"E129.MirrorCS")])]})});
            fillet(context, id + "F5", {"entities" : qUnion([Q0, Q1, Q2, Q3, Q4, Q5, Q6, Q7, Q8, Q9, Q10, Q11, Q12, Q13, Q14, Q15, Q16, Q17, Q18, Q19]), "radius" : 2 * mm, "tangentPropagation" : true, "allowEdgeOverflow" : false});
        }
    });
